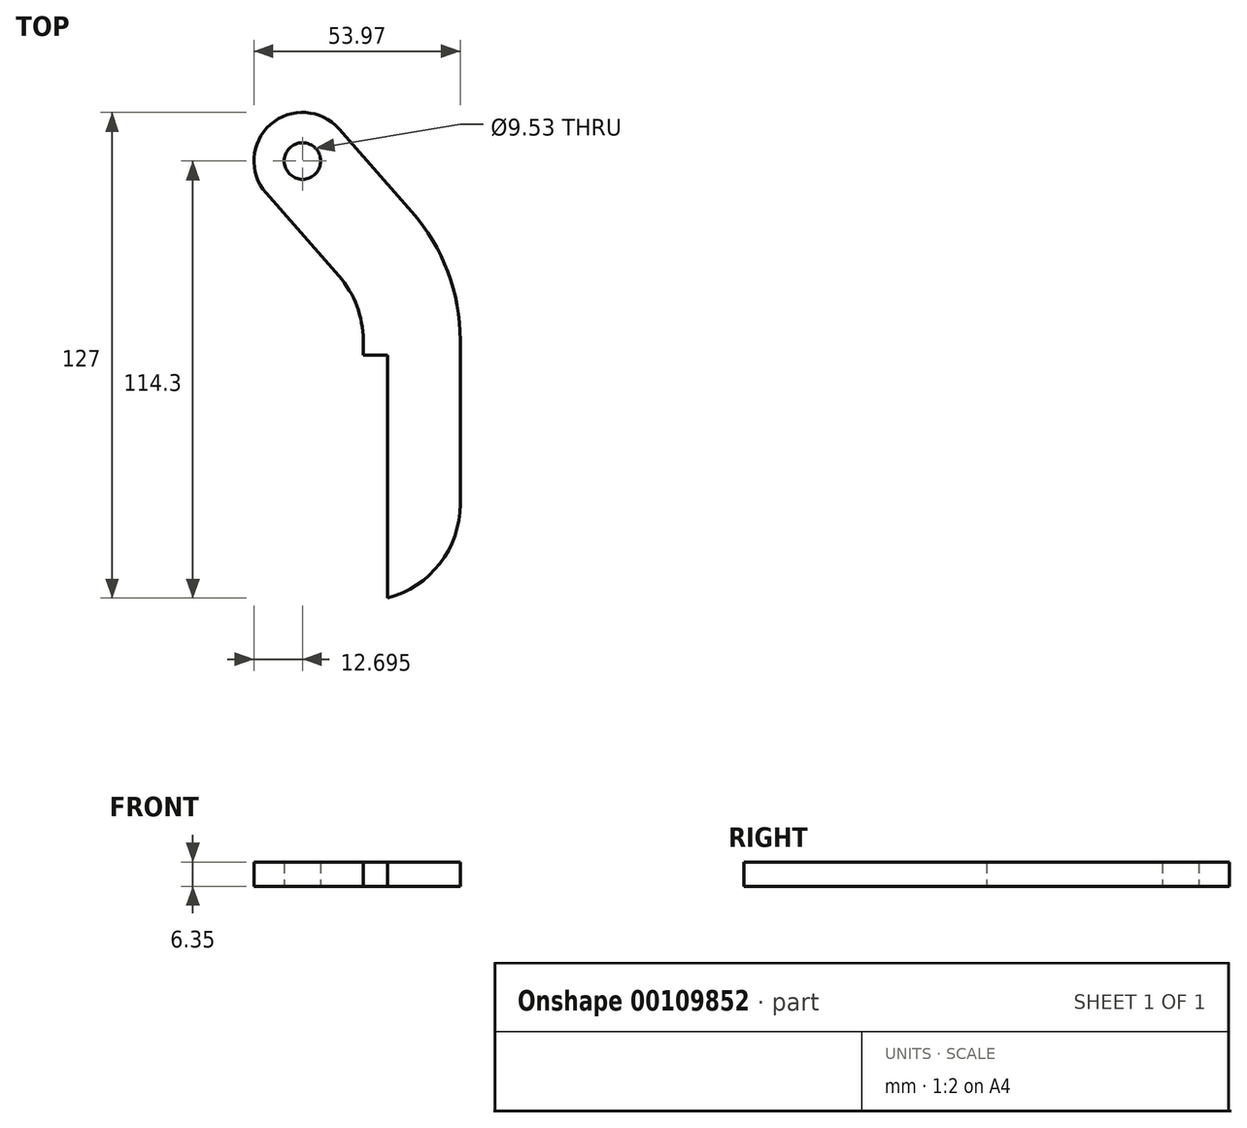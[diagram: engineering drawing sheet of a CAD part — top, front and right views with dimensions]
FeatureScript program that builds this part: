
annotation { "Feature Type Name" : "Feature", "Feature Type Description" : "" }
export const myFeature = defineFeature(function(context is Context, id is Id, definition is map)
    precondition{}
    {
        {
            var Q0;
            Q0=qCreatedBy(makeId("Top.planeOp"),FACE);
            var sketch = newSketch(context, id + "F0", { "sketchPlane" : qUnion([Q0])});
            skCircle(sketch, "E0", {"center": v(-15.88, 50.8) * mm, "radius": 4.76 * mm});
            skLineSegment(sketch, "E1", {"start": v(25.4, 23.07) * mm, "end": v(25.4, -63.5) * mm});
            skLineSegment(sketch, "E2", {"start": v(25.4, -63.5) * mm, "end": v(6.35, -63.5) * mm});
            skLineSegment(sketch, "E3", {"start": v(6.35, -63.5) * mm, "end": v(6.35, 0) * mm});
            skLineSegment(sketch, "E4", {"start": v(6.35, 0) * mm, "end": v(0, 0) * mm});
            skPoint(sketch, "E5.end.orphan", {"position": v(0, 38.9) * mm});
            skLineSegment(sketch, "E6", {"start": v(0, 13.5) * mm, "end": v(-25.42, 42.42) * mm});
            skLineSegment(sketch, "E7.0", {"start": v(25.4, 23.07) * mm, "end": v(-6.33, 59.18) * mm});
            skArc(sketch, "E8", {"start": v(-6.33, 59.18) * mm, "mid": v(-24.26, 60.34) * mm, "end": v(-25.42, 42.42) * mm});
            skLineSegment(sketch, "E9", {"start": v(0, 13.5) * mm, "end": v(0, 0) * mm});
            skSolve(sketch);
        }
        {
            var Q0;
            Q0 = qSketchRegion(id + "F0", true);
            extrude(context, id + "F1", {"entities" : qUnion([Q0]), "depth" : 6.35 * mm});
        }
        {
            var Q0;
            Q0=makeQuery(id+"F1.opExtrude","SWEPT_EDGE",EDGE,{"disambiguationData":[OSD([sQuery(id+"F0.wireOp",EDGE,"E6"),sQuery(id+"F0.wireOp",EDGE,"E9")])]});
            var Q1;
            Q1=makeQuery(id+"F1.opExtrude","SWEPT_EDGE",EDGE,{"disambiguationData":[OSD([sQuery(id+"F0.wireOp",EDGE,"E1"),sQuery(id+"F0.wireOp",EDGE,"E2")])]});
            fillet(context, id + "F2", {"entities" : qUnion([Q0, Q1]), "radius" : 25.4 * mm, "tangentPropagation" : true, "allowEdgeOverflow" : false});
        }
        {
            var Q0;
            Q0=makeQuery(id+"F1.opExtrude","SWEPT_EDGE",EDGE,{"disambiguationData":[OSD([sQuery(id+"F0.wireOp",EDGE,"E1"),sQuery(id+"F0.wireOp",EDGE,"E7.0")])]});
            fillet(context, id + "F3", {"entities" : qUnion([Q0]), "radius" : 50.8 * mm, "tangentPropagation" : true, "allowEdgeOverflow" : false});
        }
    });
